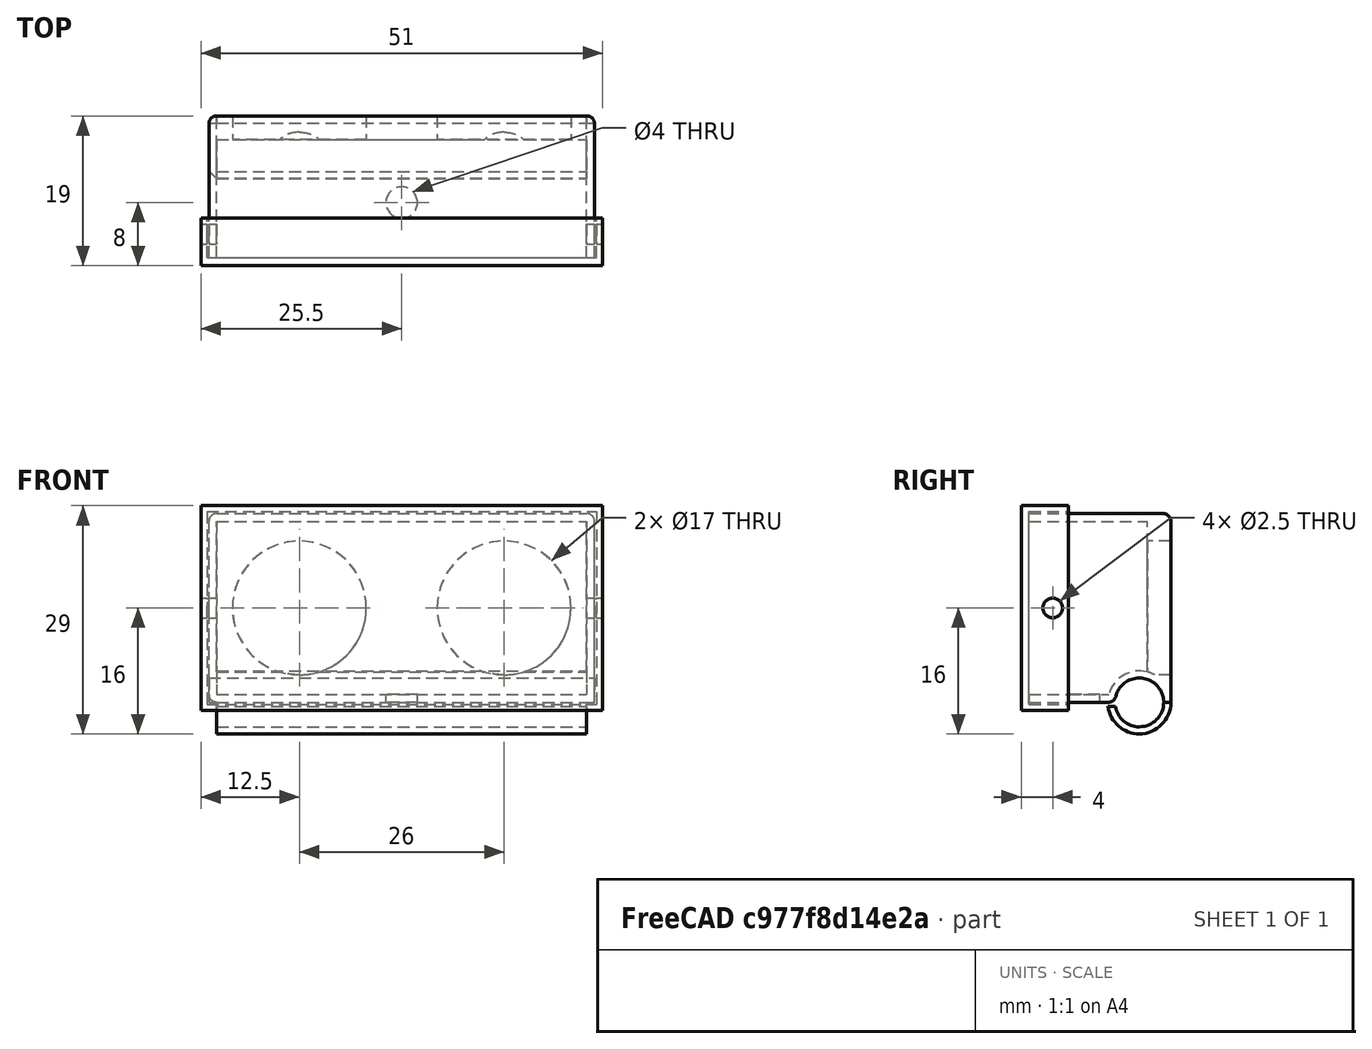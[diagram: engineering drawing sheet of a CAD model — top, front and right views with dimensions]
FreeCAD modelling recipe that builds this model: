
FCSTD DOCUMENT  (FreeCAD 0.16R6703 (Git))
Label: Ultrasound_holder_v3.0
License: CreativeCommons Attribution-ShareAlike
LicenseURL: http://creativecommons.org/licenses/by-sa/4.0/
objects: Part::Cut×8, Part::Cylinder×7, Part::Box×5, Part::MultiFuse×2, Part::Fillet×1
note: 23 computed .brp shape members not serialized (recipe doc carries the construction recipe); baked Part::Feature solids carry a one-line shape summary decoded from their .brp

FEATURE [Part::Cylinder] Cylinder  label="ultraSoun1"
  Angle = 360
  Height = 20
  Placement = pos=(-13,10,0) rot=(1,0,0;1.5708rad)
  Radius = 8.5
FEATURE [Part::Cylinder] Cylinder001  label="ultraSoun002"
  Angle = 360
  Height = 20
  Placement = pos=(13,10,0) rot=(1,0,0;1.5708rad)
  Radius = 8.5
FEATURE [Part::Box] Box  label="base"
  Height = 24
  Length = 49
  Placement = pos=(-24.5,-9,-12) rot=(0,0,1;0rad)
  Width = 18
FEATURE [Part::MultiFuse] Fusion  label="2xUltrasonidos"
  Shapes = -> [Cylinder,Cylinder001]
FEATURE [Part::Box] Box001  label="recote base"
  Height = 22
  Length = 47
  Placement = pos=(-23.5,-10,-11) rot=(0,0,1;0rad)
  Width = 16
FEATURE [Part::Cut] Cut
  Base = -> Box
  Tool = -> Box001
FEATURE [Part::Cut] Cut001
  Base = -> Cut
  Tool = -> Fusion
FEATURE [Part::Cylinder] Cylinder002  label="Cylinder"
  Angle = 360
  Height = 50
  Placement = pos=(-25,5,-12) rot=(0,1,0;1.5708rad)
  Radius = 3.1
FEATURE [Part::Cylinder] Cylinder003  label="Cylinder001"
  Angle = 360
  Height = 47
  Placement = pos=(-23.5,5,-12) rot=(0,1,0;1.5708rad)
  Radius = 4
FEATURE [Part::MultiFuse] Fusion001
  Shapes = -> [Cylinder003,Cut001]
FEATURE [Part::Cut] Cut002
  Base = -> Fusion001
  Tool = -> Cylinder002
FEATURE [Part::Box] Box002  label="Cube"
  Height = 0.5
  Length = 48
  Placement = pos=(-24,0,-12.5) rot=(0,0,1;0rad)
  Width = 3
FEATURE [Part::Cut] Cut003
  Base = -> Cut002
  Tool = -> Box002
FEATURE [Part::Cylinder] Cylinder004  label="Cylinder002"
  Angle = 360
  Height = 50
  Placement = pos=(-25,-6,0) rot=(0,1,0;1.5708rad)
  Radius = 1.25
FEATURE [Part::Cut] Cut004
  Base = -> Cut003
  Tool = -> Cylinder004
FEATURE [Part::Cylinder] Cylinder005  label="Cylinder003"
  Angle = 360
  Height = 10
  Placement = pos=(0,-2,-17) rot=(0,0,1;0rad)
  Radius = 2
FEATURE [Part::Cut] Cut005
  Base = -> Cut004
  Tool = -> Cylinder005
FEATURE [Part::Fillet] Fillet
  Base = -> Cut005
  Edges = 7 edges r=1: [Edge1,Edge2,Edge5,Edge8,Edge9,Edge14,Edge25]
FEATURE [Part::Box] Box003  label="base001"
  Height = 24.5
  Length = 49.5
  Placement = pos=(-24.75,-9,-12.25) rot=(0,0,1;0rad)
  Width = 18
FEATURE [Part::Cylinder] Cylinder006  label="Cylinder004"
  Angle = 360
  Height = 60
  Placement = pos=(-30,-6,0) rot=(0,1,0;1.5708rad)
  Radius = 1.25
FEATURE [Part::Box] Box004  label="Tapa"
  Height = 26
  Length = 51
  Placement = pos=(-25.5,-10,-13) rot=(0,0,1;0rad)
  Width = 6
FEATURE [Part::Cut] Cut006
  Base = -> Box004
  Tool = -> Box003
FEATURE [Part::Cut] Cut007  label="Cover"
  Base = -> Cut006
  Tool = -> Cylinder006
